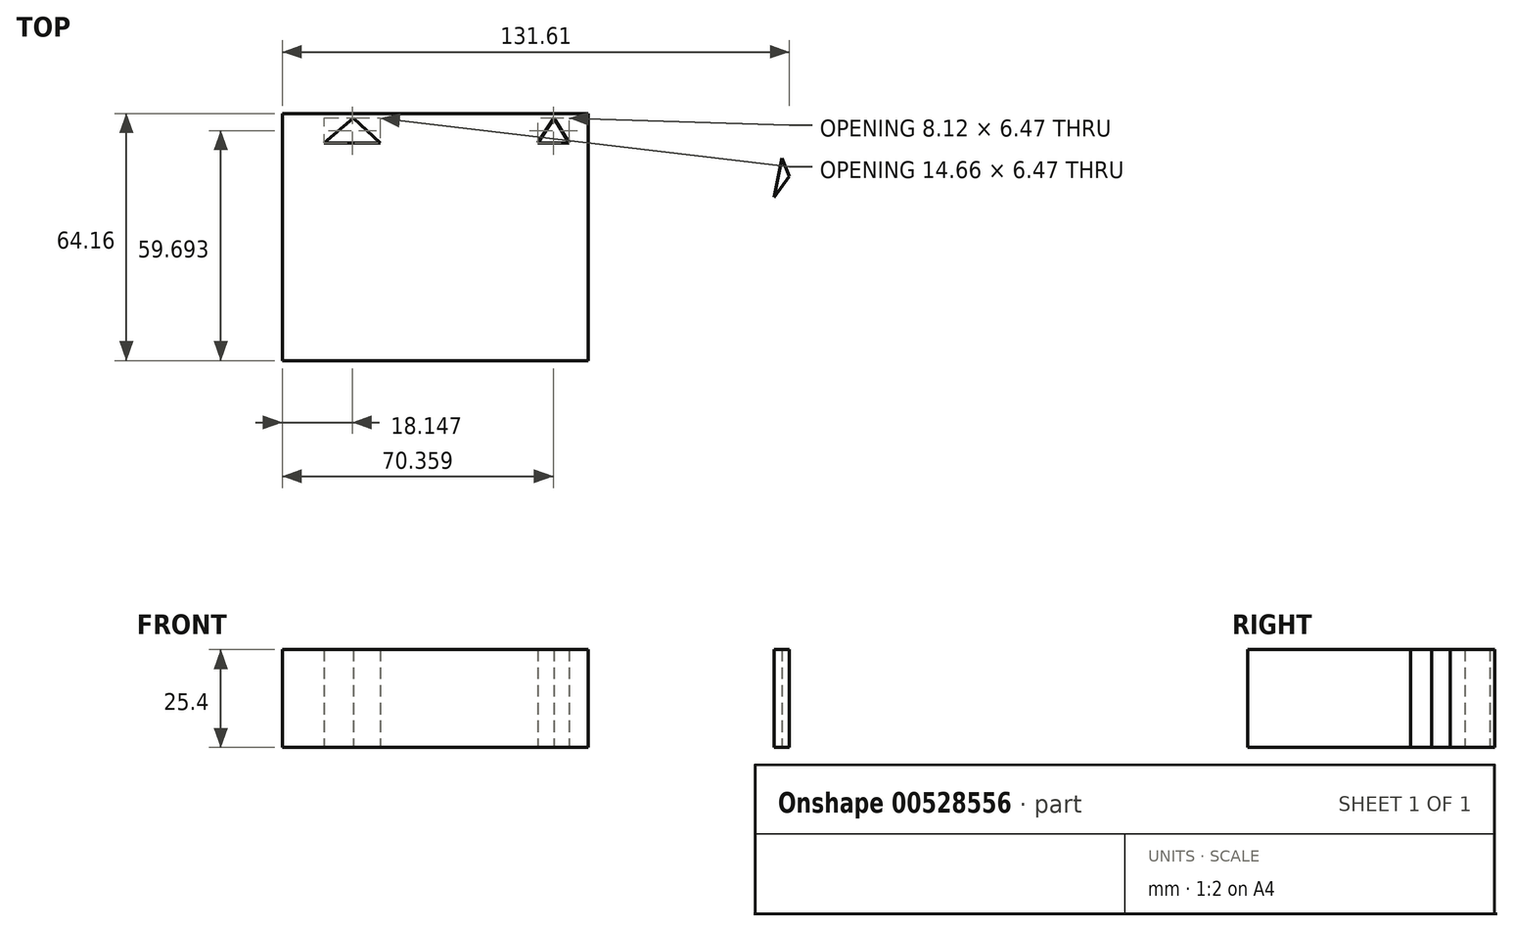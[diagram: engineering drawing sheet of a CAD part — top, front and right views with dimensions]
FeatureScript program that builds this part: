
annotation { "Feature Type Name" : "Feature", "Feature Type Description" : "" }
export const myFeature = defineFeature(function(context is Context, id is Id, definition is map)
    precondition{}
    {
        {
            var Q0;
            Q0=qCreatedBy(makeId("Top.planeOp"),FACE);
            var sketch = newSketch(context, id + "F0", { "sketchPlane" : qUnion([Q0])});
            skLineSegment(sketch, "E0", {"start": v(-28.04, 25.39) * mm, "end": v(35.56, 25.39) * mm});
            skLineSegment(sketch, "E1", {"start": v(35.56, 25.39) * mm, "end": v(35.56, -21.35) * mm});
            skLineSegment(sketch, "E2", {"start": v(35.56, -21.35) * mm, "end": v(-28.78, -21.35) * mm});
            skLineSegment(sketch, "E3", {"start": v(-28.78, -20.25) * mm, "end": v(-28.04, 25.39) * mm});
            skLineSegment(sketch, "E4", {"start": v(-28.04, 25.39) * mm, "end": v(-38.86, 33.09) * mm});
            skLineSegment(sketch, "E5", {"start": v(-38.86, 33.09) * mm, "end": v(-38.86, -31.07) * mm});
            skLineSegment(sketch, "E6", {"start": v(-40.14, -31.07) * mm, "end": v(-28.78, -21.35) * mm});
            skLineSegment(sketch, "E7", {"start": v(-38.86, 33.09) * mm, "end": v(40.5, 33.09) * mm});
            skLineSegment(sketch, "E8", {"start": v(40.5, 33.09) * mm, "end": v(35.56, 25.39) * mm});
            skLineSegment(sketch, "E9", {"start": v(40.5, 33.09) * mm, "end": v(40.5, -31.07) * mm});
            skLineSegment(sketch, "E10", {"start": v(40.5, -31.07) * mm, "end": v(35.56, -21.35) * mm});
            skLineSegment(sketch, "E11", {"start": v(-28.78, -21.35) * mm, "end": v(-20.47, -31.07) * mm});
            skLineSegment(sketch, "E12", {"start": v(-20.47, -31.07) * mm, "end": v(-11.36, -21.35) * mm});
            skLineSegment(sketch, "E13", {"start": v(-11.36, -21.35) * mm, "end": v(-3.06, -31.07) * mm});
            skLineSegment(sketch, "E14", {"start": v(-3.06, -31.07) * mm, "end": v(3.86, -21.35) * mm});
            skLineSegment(sketch, "E15", {"start": v(3.86, -21.35) * mm, "end": v(12.16, -31.07) * mm});
            skLineSegment(sketch, "E16", {"start": v(12.16, -31.07) * mm, "end": v(19.08, -21.35) * mm});
            skLineSegment(sketch, "E17", {"start": v(19.08, -21.35) * mm, "end": v(25.85, -31.07) * mm});
            skLineSegment(sketch, "E18", {"start": v(25.85, -31.07) * mm, "end": v(35.56, -21.35) * mm});
            skLineSegment(sketch, "E19", {"start": v(-38.86, -31.07) * mm, "end": v(-20.47, -31.07) * mm});
            skLineSegment(sketch, "E20", {"start": v(-3.06, -31.07) * mm, "end": v(12.16, -31.07) * mm});
            skLineSegment(sketch, "E21", {"start": v(-3.06, -31.07) * mm, "end": v(-20.47, -31.07) * mm});
            skLineSegment(sketch, "E22", {"start": v(12.16, -31.07) * mm, "end": v(40.5, -31.07) * mm});
            skLineSegment(sketch, "E23", {"start": v(-28.04, 25.39) * mm, "end": v(-20.47, 31.86) * mm});
            skLineSegment(sketch, "E24", {"start": v(-20.47, 31.86) * mm, "end": v(-13.38, 25.39) * mm});
            skLineSegment(sketch, "E25", {"start": v(-13.38, 25.39) * mm, "end": v(-6.36, 33.09) * mm});
            skLineSegment(sketch, "E26", {"start": v(-6.36, 33.09) * mm, "end": v(0.23, 25.39) * mm});
            skLineSegment(sketch, "E27", {"start": v(0.23, 25.39) * mm, "end": v(7.25, 33.09) * mm});
            skLineSegment(sketch, "E28", {"start": v(7.25, 33.09) * mm, "end": v(13.83, 25.39) * mm});
            skLineSegment(sketch, "E29", {"start": v(13.83, 25.39) * mm, "end": v(20.86, 33.09) * mm});
            skLineSegment(sketch, "E30", {"start": v(20.86, 33.09) * mm, "end": v(27.44, 25.39) * mm});
            skLineSegment(sketch, "E31", {"start": v(27.44, 25.39) * mm, "end": v(31.6, 31.86) * mm});
            skLineSegment(sketch, "E32", {"start": v(31.6, 31.86) * mm, "end": v(35.56, 25.39) * mm});
            skLineSegment(sketch, "E33", {"start": v(-20.47, 31.86) * mm, "end": v(-21.52, 33.09) * mm});
            skLineSegment(sketch, "E34", {"start": v(-21.52, 33.09) * mm, "end": v(31.6, 33.09) * mm});
            skLineSegment(sketch, "E35", {"start": v(31.6, 33.09) * mm, "end": v(31.6, 31.86) * mm});
            skLineSegment(sketch, "E36", {"start": v(92.75, 16.77) * mm, "end": v(88.83, 11.27) * mm});
            skLineSegment(sketch, "E37", {"start": v(88.83, 11.27) * mm, "end": v(90.8, 21.54) * mm});
            skPoint(sketch, "E37.endSnap0", {"position": v(90.8, 14.02) * mm});
            skLineSegment(sketch, "E38", {"start": v(90.8, 21.54) * mm, "end": v(92.75, 16.77) * mm});
            skSolve(sketch);
        }
        {
            var Q0;
            Q0 = qSketchRegion(id + "F0", true);
            extrude(context, id + "F1", {"entities" : qUnion([Q0]), "depth" : 25.4 * mm, "offsetDistance" : 25.4 * mm});
        }
    });
